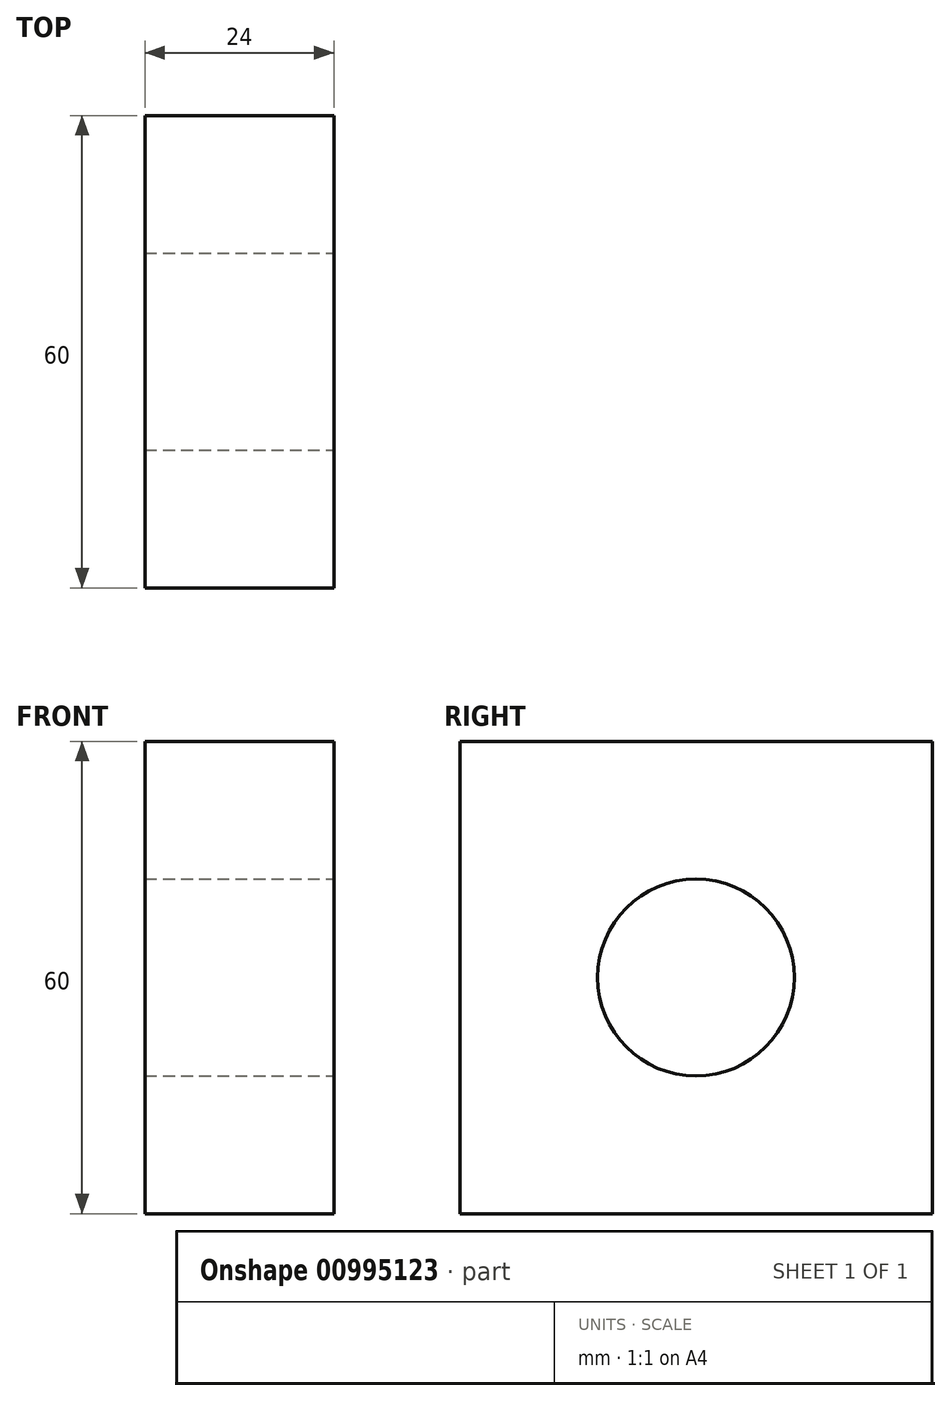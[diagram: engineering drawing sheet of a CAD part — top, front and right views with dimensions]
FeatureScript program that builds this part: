
annotation { "Feature Type Name" : "Feature", "Feature Type Description" : "" }
export const myFeature = defineFeature(function(context is Context, id is Id, definition is map)
    precondition{}
    {
        {
            var Q0;
            Q0=qCreatedBy(makeId("Front.planeOp"),FACE);
            var sketch = newSketch(context, id + "F0", { "sketchPlane" : qUnion([Q0])});
            skLineSegment(sketch, "E0", {"start": v(-380, 0) * mm, "end": v(-380, 350) * mm, "construction": true});
            skLineSegment(sketch, "E1", {"start": v(-380, 350) * mm, "end": v(0, 480) * mm, "construction": true});
            skLineSegment(sketch, "E2", {"start": v(0, 480) * mm, "end": v(380, 350) * mm, "construction": true});
            skLineSegment(sketch, "E3", {"start": v(380, 350) * mm, "end": v(380, 0) * mm, "construction": true});
            skLineSegment(sketch, "E4", {"start": v(380, 0) * mm, "end": v(280, 0) * mm, "construction": true});
            skLineSegment(sketch, "E5", {"start": v(280, 0) * mm, "end": v(280, 280) * mm, "construction": true});
            skLineSegment(sketch, "E6", {"start": v(280, 280) * mm, "end": v(-256, 280) * mm, "construction": true});
            skLineSegment(sketch, "E7", {"start": v(-280, 280) * mm, "end": v(-280, 220) * mm});
            skLineSegment(sketch, "E8", {"start": v(-280, 0) * mm, "end": v(-380, 0) * mm, "construction": true});
            skLineSegment(sketch, "E9.bottom", {"start": v(-280, 280) * mm, "end": v(-256, 280) * mm});
            skLineSegment(sketch, "E9.top", {"start": v(-280, 220) * mm, "end": v(-256, 220) * mm});
            skLineSegment(sketch, "E9.right", {"start": v(-256, 280) * mm, "end": v(-256, 220) * mm});
            skLineSegment(sketch, "E10", {"start": v(-256, 280) * mm, "end": v(-280, 280) * mm});
            skLineSegment(sketch, "E11", {"start": v(-280, 220) * mm, "end": v(-280, 0) * mm, "construction": true});
            skSolve(sketch);
        }
        {
            var Q0;
            Q0=makeQuery(id+"F0.imprint","IMPRINT",FACE,{"disambiguationData":[TD([[makeQuery(id+"F0.imprint","IMPRINT",EDGE,{"derivedFrom":sQuery(id+"F0.wireOp",EDGE,"E9.top")}),1.0]])]});
            extrude(context, id + "F1", {"entities" : qUnion([Q0]), "oppositeDirection" : true, "depth" : 60 * mm, "offsetDistance" : 25 * mm});
        }
        {
            var Q0;
            Q0=makeQuery(id+"F1.opExtrude","SWEPT_FACE",FACE,{"disambiguationData":[OSD([sQuery(id+"F0.wireOp",EDGE,"E9.right")])]});
            var sketch = newSketch(context, id + "F2", { "sketchPlane" : qUnion([Q0])});
            skCircle(sketch, "E12", {"center": v(30, 250) * mm, "radius": 12.5 * mm});
            skSolve(sketch);
        }
        {
            var Q0;
            Q0 = qSketchRegion(id + "F2", true);
            extrude(context, id + "F3", {"entities" : qUnion([Q0]), "operationType" : NewBodyOperationType.REMOVE, "oppositeDirection" : true, "depth" : 25 * mm, "offsetDistance" : 25 * mm});
        }
    });
